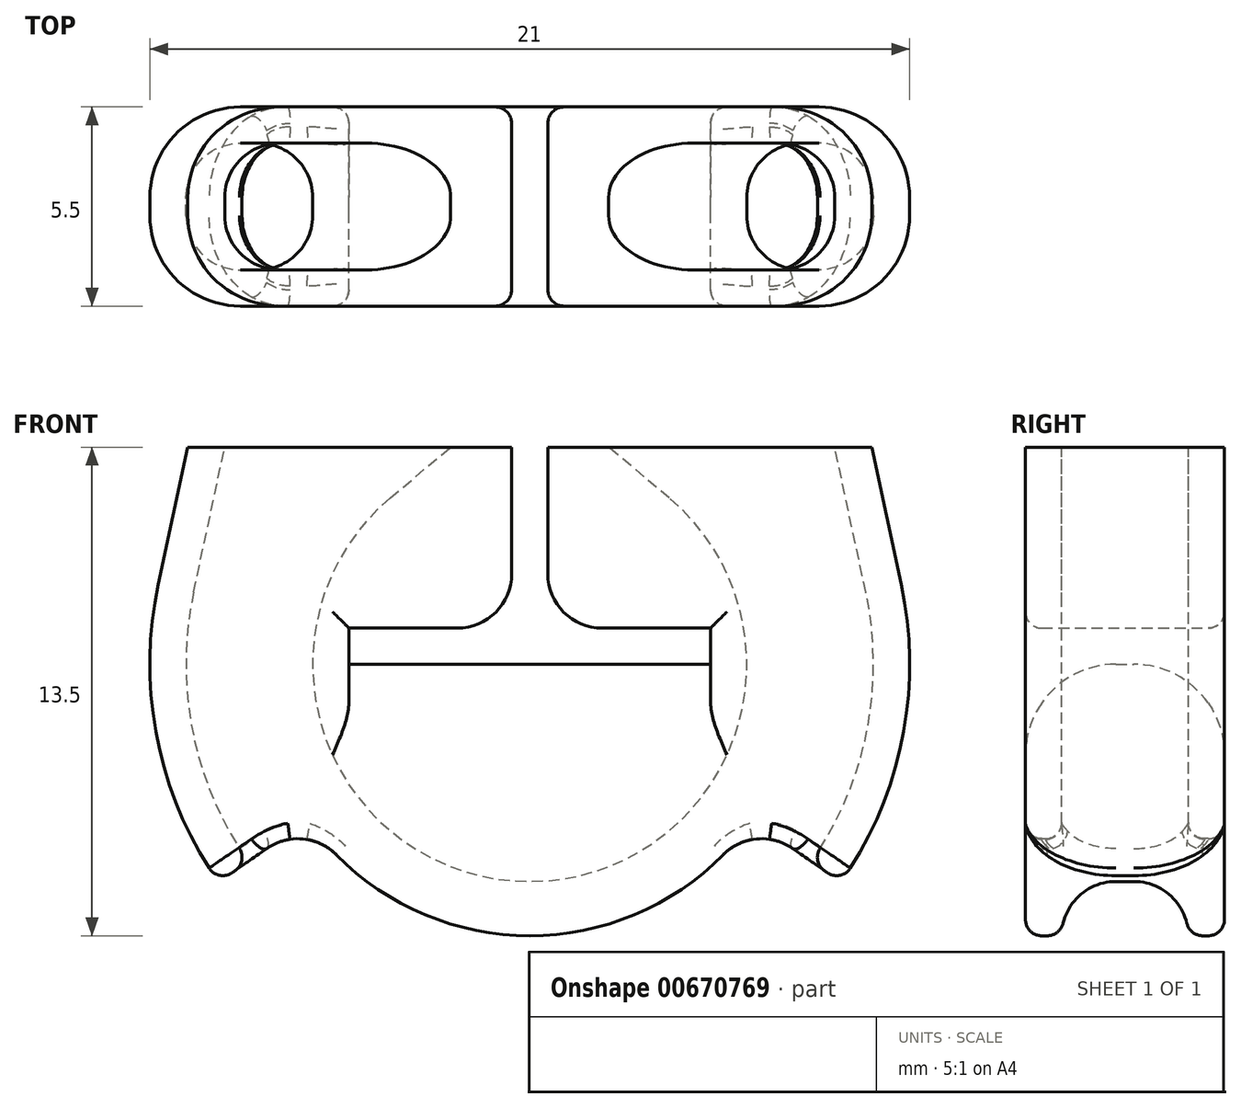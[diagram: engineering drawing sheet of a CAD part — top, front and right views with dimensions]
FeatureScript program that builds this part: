
annotation { "Feature Type Name" : "Feature", "Feature Type Description" : "" }
export const myFeature = defineFeature(function(context is Context, id is Id, definition is map)
    precondition{}
    {
        {
            var Q0;
            Q0=qCreatedBy(makeId("Front.planeOp"),FACE);
            var sketch = newSketch(context, id + "F0", { "sketchPlane" : qUnion([Q0])});
            skLineSegment(sketch, "E0.bottom", {"start": v(0, 0) * mm, "end": v(5, 0) * mm});
            skLineSegment(sketch, "E0.top", {"start": v(0, 1) * mm, "end": v(5, 1) * mm});
            skLineSegment(sketch, "E0.left", {"start": v(0, 0) * mm, "end": v(0, 1) * mm});
            skLineSegment(sketch, "E0.right", {"start": v(5, 0) * mm, "end": v(5, 1) * mm});
            skSolve(sketch);
        }
        {
            var Q0;
            Q0=qCreatedBy(makeId("Front.planeOp"),FACE);
            var sketch = newSketch(context, id + "F1", { "sketchPlane" : qUnion([Q0])});
            skArc(sketch, "E1", {"start": v(0, -10.5) * mm, "mid": v(8.17, -6.6) * mm, "end": v(10.27, 2.2) * mm});
            skLineSegment(sketch, "E2", {"start": v(10.27, 2.2) * mm, "end": v(9.45, 6) * mm});
            skLineSegment(sketch, "E3", {"start": v(9.45, 6) * mm, "end": v(0, 6) * mm});
            skLineSegment(sketch, "E4", {"start": v(0, 6) * mm, "end": v(0, -10.5) * mm});
            skPoint(sketch, "E5", {"position": v(10.5, 0) * mm});
            skPoint(sketch, "E6", {"position": v(0, 50) * mm});
            skSolve(sketch);
        }
        {
            var Q0;
            Q0 = qSketchRegion(id + "F1", true);
            extrude(context, id + "F2", {"entities" : qUnion([Q0]), "depth" : 2.75 * mm, "offsetDistance" : 25 * mm});
        }
        {
            var Q0;
            Q0=qCreatedBy(makeId("Front.planeOp"),FACE);
            var sketch = newSketch(context, id + "F3", { "sketchPlane" : qUnion([Q0])});
            skArc(sketch, "E7", {"start": v(0, -6) * mm, "mid": v(5.64, -2.05) * mm, "end": v(3.86, 4.6) * mm});
            skArc(sketch, "E8.1", {"start": v(0, -9.5) * mm, "mid": v(7.39, -5.97) * mm, "end": v(9.29, 2) * mm});
            skLineSegment(sketch, "E9", {"start": v(9.29, 2) * mm, "end": v(8.43, 6) * mm});
            skLineSegment(sketch, "E10", {"start": v(3.86, 4.6) * mm, "end": v(2.18, 6) * mm});
            skPoint(sketch, "E11", {"position": v(6, 0) * mm});
            skPoint(sketch, "E12", {"position": v(9.5, 0) * mm});
            skLineSegment(sketch, "E13", {"start": v(0, -6) * mm, "end": v(0, -9.5) * mm});
            skLineSegment(sketch, "E14", {"start": v(2.18, 6) * mm, "end": v(8.43, 6) * mm});
            skSolve(sketch);
        }
        {
            var Q0;
            Q0 = qSketchRegion(id + "F3", true);
            extrude(context, id + "F4", {"entities" : qUnion([Q0]), "operationType" : NewBodyOperationType.REMOVE, "depth" : 1.75 * mm, "offsetDistance" : 25 * mm});
        }
        {
            var Q0;
            Q0=qCreatedBy(makeId("Front.planeOp"),FACE);
            var sketch = newSketch(context, id + "F5", { "sketchPlane" : qUnion([Q0])});
            skLineSegment(sketch, "E15.0", {"start": v(0.5, 1) * mm, "end": v(5, 1) * mm});
            skPoint(sketch, "E16.0", {"position": v(5, 0) * mm});
            skLineSegment(sketch, "E17.0", {"start": v(5, 0) * mm, "end": v(5, 1) * mm});
            skLineSegment(sketch, "E18.0", {"start": v(0, 0) * mm, "end": v(5, 0) * mm});
            skLineSegment(sketch, "E19", {"start": v(0.5, 6) * mm, "end": v(0.5, 1) * mm});
            skLineSegment(sketch, "E20", {"start": v(0.5, 6) * mm, "end": v(0, 6) * mm});
            skLineSegment(sketch, "E21", {"start": v(0, 6) * mm, "end": v(0, 0) * mm});
            skPoint(sketch, "E22.orphan", {"position": v(0, 1) * mm});
            skSolve(sketch);
        }
        {
            var Q0;
            Q0 = qSketchRegion(id + "F5", true);
            extrude(context, id + "F6", {"entities" : qUnion([Q0]), "operationType" : NewBodyOperationType.REMOVE, "endBound" : BoundingType.THROUGH_ALL, "depth" : 25 * mm, "offsetDistance" : 25 * mm});
        }
        {
            var Q0;
            Q0=qCreatedBy(makeId("Front.planeOp"),FACE);
            var sketch = newSketch(context, id + "F7", { "sketchPlane" : qUnion([Q0])});
            skArc(sketch, "E23", {"start": v(0, -7.5) * mm, "mid": v(3.46, -6.65) * mm, "end": v(6.14, -4.3) * mm});
            skArc(sketch, "E24", {"start": v(0, -12) * mm, "mid": v(5.54, -10.64) * mm, "end": v(9.83, -6.88) * mm});
            skLineSegment(sketch, "E25", {"start": v(9.83, -6.88) * mm, "end": v(6.14, -4.3) * mm});
            skLineSegment(sketch, "E26", {"start": v(0, -12) * mm, "end": v(0, -7.5) * mm});
            skSolve(sketch);
        }
        {
            var Q0;
            Q0 = qSketchRegion(id + "F7", true);
            extrude(context, id + "F8", {"entities" : qUnion([Q0]), "operationType" : NewBodyOperationType.REMOVE, "endBound" : BoundingType.THROUGH_ALL, "depth" : 25 * mm, "offsetDistance" : 25 * mm});
        }
        {
            var Q0;
            Q0=makeQuery(id+"F6.boolean.opBoolean","INTERSECT",EDGE,{"derivedFrom":[makeQuery(id+"F2.opExtrude","CAP_FACE",FACE,{"disambiguationData":[OSD([sQuery(id+"F1.wireOp",EDGE,"E1"),sQuery(id+"F1.wireOp",EDGE,"E2"),sQuery(id+"F1.wireOp",EDGE,"E3"),sQuery(id+"F1.wireOp",EDGE,"E4")])],"isStart":false}),makeQuery(id+"F6.opExtrude","SWEPT_FACE",FACE,{"disambiguationData":[OSD([sQuery(id+"F5.wireOp",EDGE,"E18.0")])]})]});
            var Q1;
            Q1=makeQuery(id+"F2.opExtrude","CAP_EDGE",EDGE,{"disambiguationData":[OSD([sQuery(id+"F1.wireOp",EDGE,"E1")])],"isStart":false});
            fillet(context, id + "F9", {"entities" : qUnion([Q0, Q1]), "radius" : 2.5 * mm, "tangentPropagation" : true, "allowEdgeOverflow" : false});
        }
        {
            var Q0;
            Q0=makeQuery(id+"F4.boolean.opBoolean","COPY",EDGE,{"derivedFrom":makeQuery(id+"F4.opExtrude","CAP_EDGE",EDGE,{"disambiguationData":[OSD([sQuery(id+"F3.wireOp",EDGE,"E8.1")])],"isStart":false})});
            var Q1;
            Q1=makeQuery(id+"F4.boolean.opBoolean","COPY",EDGE,{"derivedFrom":makeQuery(id+"F4.opExtrude","CAP_EDGE",EDGE,{"disambiguationData":[OSD([sQuery(id+"F3.wireOp",EDGE,"E7")])],"isStart":false})});
            fillet(context, id + "F10", {"entities" : qUnion([Q0, Q1]), "radius" : 1.5 * mm, "tangentPropagation" : true, "allowEdgeOverflow" : false});
        }
        {
            var Q0;
            Q0=makeQuery(id+"F6.boolean.opBoolean","COPY",EDGE,{"derivedFrom":makeQuery(id+"F6.opExtrude","SWEPT_EDGE",EDGE,{"disambiguationData":[OSD([sQuery(id+"F5.wireOp",EDGE,"E15.0"),sQuery(id+"F5.wireOp",EDGE,"E19")])]})});
            var Q1;
            Q1=makeQuery(id+"F6.boolean.opBoolean","COPY",EDGE,{"derivedFrom":makeQuery(id+"F6.opExtrude","SWEPT_EDGE",EDGE,{"disambiguationData":[OSD([sQuery(id+"F5.wireOp",EDGE,"E19"),sQuery(id+"F5.wireOp",EDGE,"E20")])]})});
            var Q2;
            Q2=makeQuery(id+"F8.boolean.opBoolean","COPY",EDGE,{"derivedFrom":makeQuery(id+"F8.opExtrude","SWEPT_EDGE",EDGE,{"disambiguationData":[OSD([sQuery(id+"F7.wireOp",EDGE,"E23"),sQuery(id+"F7.wireOp",EDGE,"E25")])]})});
            fillet(context, id + "F11", {"entities" : qUnion([Q0, Q1, Q2]), "radius" : 1.5 * mm, "tangentPropagation" : true, "allowEdgeOverflow" : false});
        }
        {
            var Q0;
            Q0=makeQuery(id+"F10.opFillet","BLEND_EDGE",EDGE,{"blendedFrom":[makeQuery(id+"F4.boolean.opBoolean","COPY",EDGE,{"derivedFrom":makeQuery(id+"F4.opExtrude","CAP_EDGE",EDGE,{"disambiguationData":[OSD([sQuery(id+"F3.wireOp",EDGE,"E7")])],"isStart":false})}),makeQuery(id+"F8.boolean.opBoolean","COPY",FACE,{"derivedFrom":makeQuery(id+"F8.opExtrude","SWEPT_FACE",FACE,{"disambiguationData":[OSD([sQuery(id+"F7.wireOp",EDGE,"E23")])]})})],"blendedInto":[makeQuery(id+"F8.boolean.opBoolean","COPY",FACE,{"derivedFrom":makeQuery(id+"F8.opExtrude","SWEPT_FACE",FACE,{"disambiguationData":[OSD([sQuery(id+"F7.wireOp",EDGE,"E23")])]})})]});
            var Q1;
            Q1=makeQuery(id+"F4.boolean.opBoolean","COPY",EDGE,{"derivedFrom":makeQuery(id+"F4.opExtrude","CAP_EDGE",EDGE,{"disambiguationData":[OSD([sQuery(id+"F3.wireOp",EDGE,"E14")])],"isStart":false})});
            var Q2;
            Q2=makeQuery(id+"F6.boolean.opBoolean","INTERSECT",EDGE,{"derivedFrom":[makeQuery(id+"F2.opExtrude","CAP_FACE",FACE,{"disambiguationData":[OSD([sQuery(id+"F1.wireOp",EDGE,"E1"),sQuery(id+"F1.wireOp",EDGE,"E2"),sQuery(id+"F1.wireOp",EDGE,"E3"),sQuery(id+"F1.wireOp",EDGE,"E4")])],"isStart":false}),makeQuery(id+"F6.opExtrude","SWEPT_FACE",FACE,{"disambiguationData":[OSD([sQuery(id+"F5.wireOp",EDGE,"E17.0")])]})]});
            var Q3;
            Q3=makeQuery(id+"F6.boolean.opBoolean","INTERSECT",EDGE,{"derivedFrom":[makeQuery(id+"F2.opExtrude","CAP_FACE",FACE,{"disambiguationData":[OSD([sQuery(id+"F1.wireOp",EDGE,"E1"),sQuery(id+"F1.wireOp",EDGE,"E2"),sQuery(id+"F1.wireOp",EDGE,"E3"),sQuery(id+"F1.wireOp",EDGE,"E4")])],"isStart":false}),makeQuery(id+"F6.opExtrude","SWEPT_FACE",FACE,{"disambiguationData":[OSD([sQuery(id+"F5.wireOp",EDGE,"E15.0")])]})]});
            var Q4;
            Q4=makeQuery(id+"F8.boolean.opBoolean","INTERSECT",EDGE,{"derivedFrom":[makeQuery(id+"F2.opExtrude","CAP_FACE",FACE,{"disambiguationData":[OSD([sQuery(id+"F1.wireOp",EDGE,"E1"),sQuery(id+"F1.wireOp",EDGE,"E2"),sQuery(id+"F1.wireOp",EDGE,"E3"),sQuery(id+"F1.wireOp",EDGE,"E4")])],"isStart":false}),makeQuery(id+"F8.opExtrude","SWEPT_FACE",FACE,{"disambiguationData":[OSD([sQuery(id+"F7.wireOp",EDGE,"E23")])]})]});
            fillet(context, id + "F12", {"entities" : qUnion([Q0, Q1, Q2, Q3, Q4]), "radius" : 0.45 * mm, "tangentPropagation" : true, "allowEdgeOverflow" : false});
        }
        {
            var Q0;
            Q0=makeQuery(id+"F2.opExtrude","SWEPT_BODY",BODY,{"disambiguationData":[OSD([sQuery(id+"F1.wireOp",EDGE,"E1"),sQuery(id+"F1.wireOp",EDGE,"E2"),sQuery(id+"F1.wireOp",EDGE,"E3"),sQuery(id+"F1.wireOp",EDGE,"E4")])]});
            var Q1;
            Q1=qCreatedBy(makeId("Front.planeOp"),FACE);
            mirror(context, id + "F13", {"operationType" : NewBodyOperationType.ADD, "entities" : qUnion([Q0]), "mirrorPlane" : qUnion([Q1])});
        }
        {
            var Q0;
            Q0=makeQuery(id+"F2.opExtrude","SWEPT_BODY",BODY,{"disambiguationData":[OSD([sQuery(id+"F1.wireOp",EDGE,"E1"),sQuery(id+"F1.wireOp",EDGE,"E2"),sQuery(id+"F1.wireOp",EDGE,"E3"),sQuery(id+"F1.wireOp",EDGE,"E4")])]});
            var Q1;
            Q1=qCreatedBy(makeId("Right.planeOp"),FACE);
            mirror(context, id + "F14", {"operationType" : NewBodyOperationType.ADD, "entities" : qUnion([Q0]), "mirrorPlane" : qUnion([Q1])});
        }
    });
